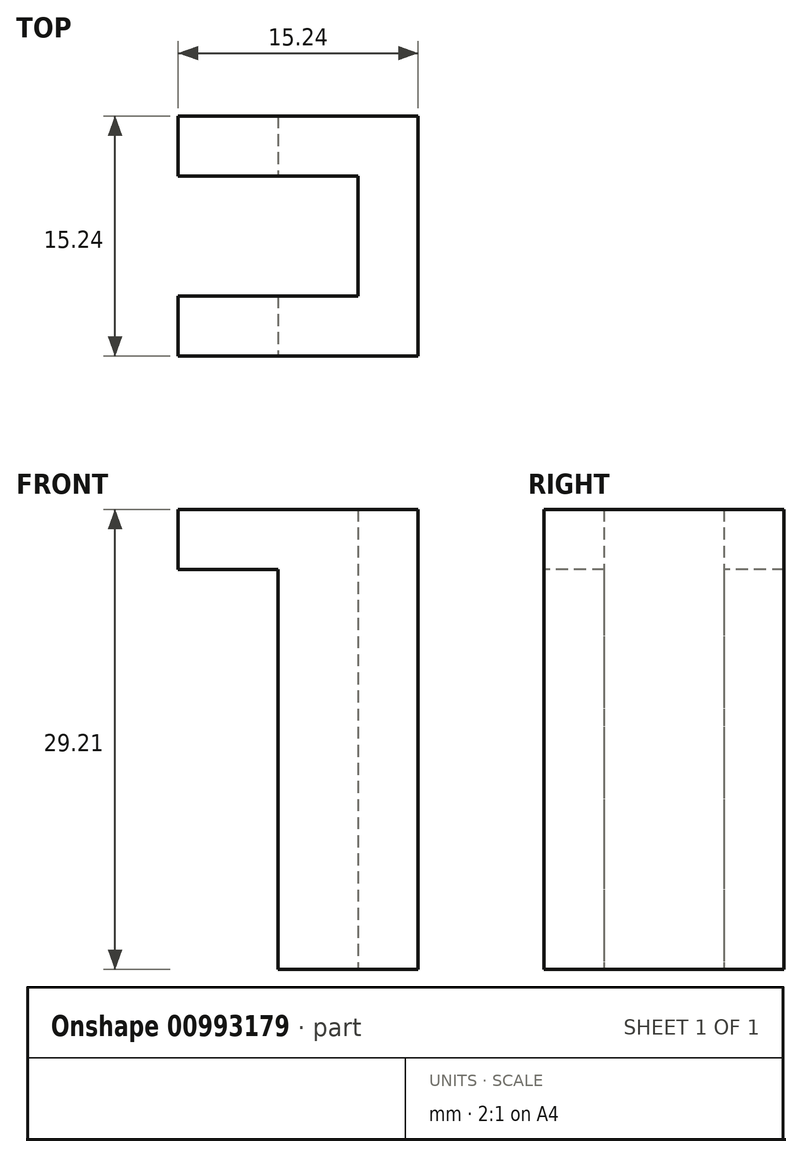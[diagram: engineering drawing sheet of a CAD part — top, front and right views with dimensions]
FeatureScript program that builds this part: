
annotation { "Feature Type Name" : "Feature", "Feature Type Description" : "" }
export const myFeature = defineFeature(function(context is Context, id is Id, definition is map)
    precondition{}
    {
        {
            var Q0;
            Q0=qCreatedBy(makeId("Top.planeOp"),FACE);
            var sketch = newSketch(context, id + "F0", { "sketchPlane" : qUnion([Q0])});
            skLineSegment(sketch, "E0.bottom", {"start": v(-45, 4.73) * mm, "end": v(-29.75, 4.73) * mm});
            skLineSegment(sketch, "E0.top", {"start": v(-45, -10.5) * mm, "end": v(-29.75, -10.5) * mm});
            skLineSegment(sketch, "E0.left", {"start": v(-45, 4.73) * mm, "end": v(-45, -10.5) * mm});
            skLineSegment(sketch, "E0.right", {"start": v(-29.75, 4.73) * mm, "end": v(-29.75, -10.5) * mm});
            skLineSegment(sketch, "E1.bottom", {"start": v(-45, 0.92) * mm, "end": v(-38.64, 0.92) * mm});
            skLineSegment(sketch, "E1.top", {"start": v(-45, -6.7) * mm, "end": v(-38.64, -6.7) * mm});
            skLineSegment(sketch, "E1.left", {"start": v(-45, 0.92) * mm, "end": v(-45, -6.7) * mm});
            skLineSegment(sketch, "E1.right", {"start": v(-38.64, 0.92) * mm, "end": v(-38.64, -6.7) * mm});
            skSolve(sketch);
        }
        {
            var Q0;
            {var subQ4=sQuery(id+"F0.wireOp",EDGE,"E0.bottom");Q0=makeQuery(id+"F0.imprint","IMPRINT",FACE,{"disambiguationData":[TD([[makeQuery(id+"F0.imprint","IMPRINT",EDGE,{"derivedFrom":subQ4}),-1.0]])]});}
            extrude(context, id + "F1", {"entities" : qUnion([Q0]), "depth" : 3.8 * mm, "offsetDistance" : 25.4 * mm});
        }
        {
            var Q0;
            Q0=makeQuery(id+"F1.opExtrude","CAP_FACE",FACE,{"disambiguationData":[OSD([sQuery(id+"F0.wireOp",EDGE,"E0.bottom"),sQuery(id+"F0.wireOp",EDGE,"E0.top"),sQuery(id+"F0.wireOp",EDGE,"E0.left"),sQuery(id+"F0.wireOp",EDGE,"E0.right"),sQuery(id+"F0.wireOp",EDGE,"E1.bottom"),sQuery(id+"F0.wireOp",EDGE,"E1.top"),sQuery(id+"F0.wireOp",EDGE,"E1.right")])],"isStart":true});
            var sketch = newSketch(context, id + "F2", { "sketchPlane" : qUnion([Q0])});
            skLineSegment(sketch, "E2.bottom", {"start": v(-38.64, 10.5) * mm, "end": v(-29.75, 10.5) * mm});
            skLineSegment(sketch, "E2.top", {"start": v(-38.64, -4.73) * mm, "end": v(-29.75, -4.73) * mm});
            skLineSegment(sketch, "E2.left", {"start": v(-38.64, 10.5) * mm, "end": v(-38.64, -4.73) * mm});
            skLineSegment(sketch, "E2.right", {"start": v(-29.75, 10.5) * mm, "end": v(-29.75, -4.73) * mm});
            skSolve(sketch);
        }
        {
            var Q0;
            {var subQ3=sQuery(id+"F2.wireOp",EDGE,"E2.bottom");Q0=makeQuery(id+"F2.imprint","IMPRINT",FACE,{"disambiguationData":[TD([[makeQuery(id+"F2.imprint","IMPRINT",EDGE,{"derivedFrom":subQ3}),-1.0]])]});}
            extrude(context, id + "F3", {"entities" : qUnion([Q0]), "operationType" : NewBodyOperationType.ADD, "depth" : 25.4 * mm, "offsetDistance" : 25.4 * mm});
        }
        {
            var Q0;
            Q0=makeQuery(id+"F3.opExtrude","CAP_FACE",FACE,{"disambiguationData":[OSD([sQuery(id+"F2.wireOp",EDGE,"E2.bottom"),sQuery(id+"F2.wireOp",EDGE,"E2.top"),sQuery(id+"F2.wireOp",EDGE,"E2.left"),sQuery(id+"F2.wireOp",EDGE,"E2.right")])],"isStart":false});
            var sketch = newSketch(context, id + "F4", { "sketchPlane" : qUnion([Q0])});
            skLineSegment(sketch, "E3.bottom", {"start": v(-38.64, -0.92) * mm, "end": v(-33.56, -0.92) * mm});
            skLineSegment(sketch, "E3.top", {"start": v(-38.64, 6.7) * mm, "end": v(-33.56, 6.7) * mm});
            skLineSegment(sketch, "E3.left", {"start": v(-38.64, -0.92) * mm, "end": v(-38.64, 6.7) * mm});
            skLineSegment(sketch, "E3.right", {"start": v(-33.56, -0.92) * mm, "end": v(-33.56, 6.7) * mm});
            skPoint(sketch, "E3.middle", {"position": v(-36.1, 2.89) * mm});
            skPoint(sketch, "E3.middle.positionSnap0", {"position": v(-38.64, 2.89) * mm});
            skPoint(sketch, "E3.centerSnap0", {"position": v(-38.64, 2.89) * mm});
            skSolve(sketch);
        }
        {
            var Q0;
            Q0=makeQuery(id+"F4.imprint","IMPRINT",FACE,{"disambiguationData":[TD([[makeQuery(id+"F4.imprint","IMPRINT",EDGE,{"derivedFrom":sQuery(id+"F4.wireOp",EDGE,"E3.bottom")}),1.0]])]});
            extrude(context, id + "F5", {"entities" : qUnion([Q0]), "operationType" : NewBodyOperationType.REMOVE, "oppositeDirection" : true, "depth" : 50.8 * mm, "offsetDistance" : 25.4 * mm});
        }
    });
